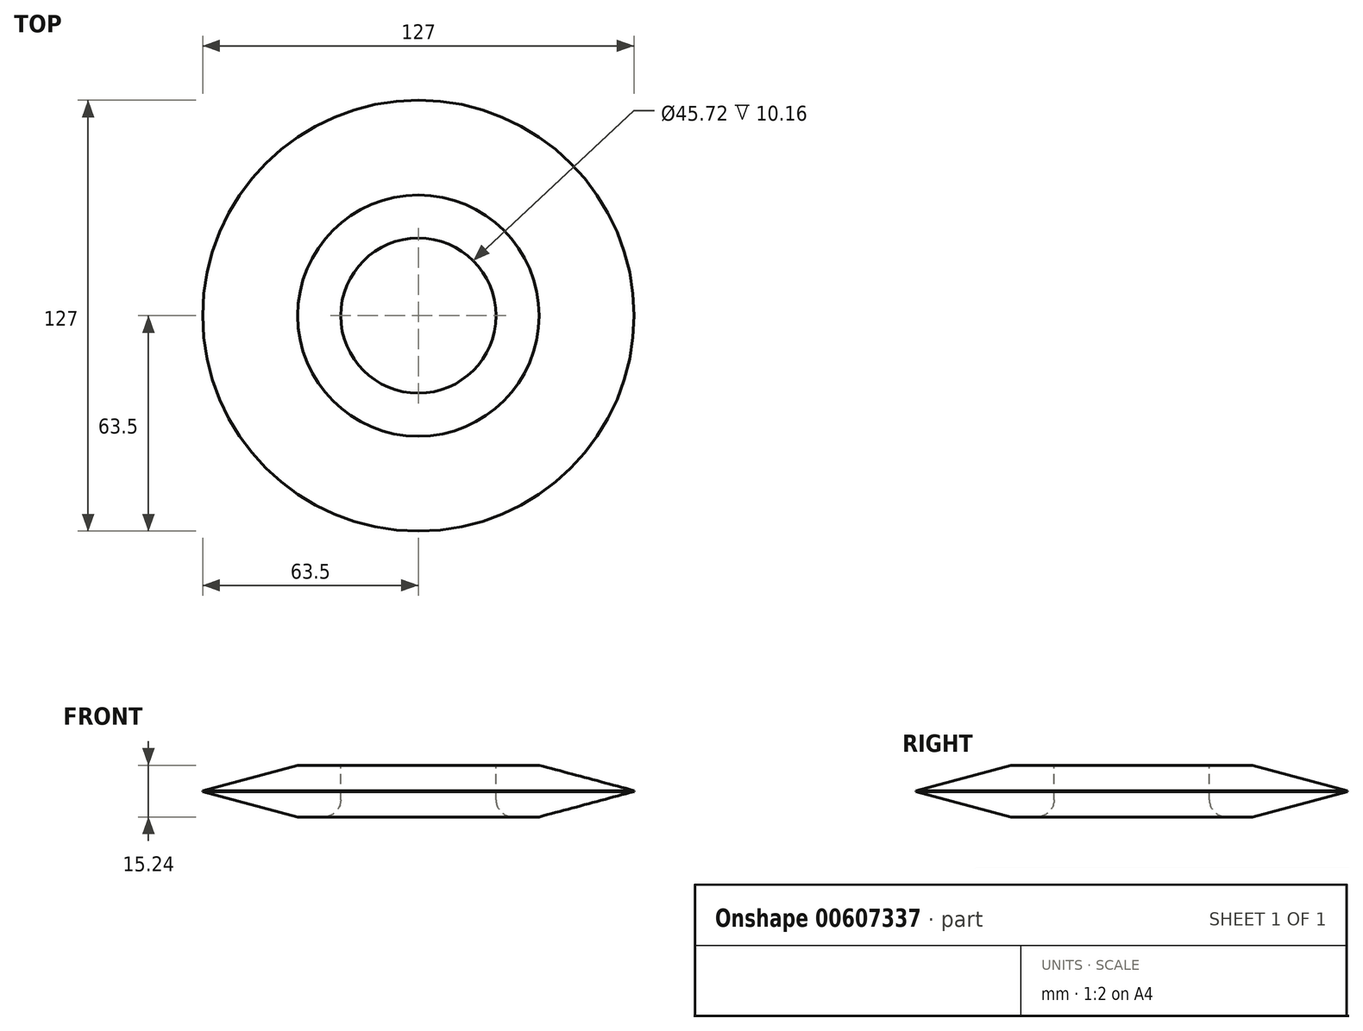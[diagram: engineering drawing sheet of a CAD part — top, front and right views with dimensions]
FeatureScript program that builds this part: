
annotation { "Feature Type Name" : "Feature", "Feature Type Description" : "" }
export const myFeature = defineFeature(function(context is Context, id is Id, definition is map)
    precondition{}
    {
        {
            var Q0;
            Q0=qCreatedBy(makeId("Top.planeOp"),FACE);
            var sketch = newSketch(context, id + "F0", { "sketchPlane" : qUnion([Q0])});
            skCircle(sketch, "E0", {"center": v(0, 0) * mm, "radius": 63.5 * mm});
            skSolve(sketch);
        }
        {
            var Q0;
            Q0 = qSketchRegion(id + "F0", true);
            extrude(context, id + "F1", {"entities" : qUnion([Q0]), "depth" : 15.24 * mm, "offsetDistance" : 25.4 * mm});
        }
        {
            var Q0;
            Q0=makeQuery(id+"F1.opExtrude","CAP_EDGE",EDGE,{"disambiguationData":[OSD([sQuery(id+"F0.wireOp",EDGE,"E0")])],"isStart":false});
            var Q1;
            Q1=makeQuery(id+"F1.opExtrude","SWEPT_FACE",FACE,{"disambiguationData":[OSD([sQuery(id+"F0.wireOp",EDGE,"E0")])]});
            chamfer(context, id + "F2", {"entities" : qUnion([Q0, Q1]), "chamferType" : ChamferType.OFFSET_ANGLE, "width" : 27.94 * mm, "oppositeDirection" : false, "angle" : 15 * degree, "tangentPropagation" : true});
        }
        {
            var Q0;
            Q0=makeQuery(id+"F1.opExtrude","CAP_FACE",FACE,{"disambiguationData":[OSD([sQuery(id+"F0.wireOp",EDGE,"E0")])],"isStart":false});
            var sketch = newSketch(context, id + "F3", { "sketchPlane" : qUnion([Q0])});
            skCircle(sketch, "E1", {"center": v(0, 0) * mm, "radius": 22.86 * mm});
            skSolve(sketch);
        }
        {
            var Q0;
            Q0 = qSketchRegion(id + "F3", true);
            extrude(context, id + "F4", {"entities" : qUnion([Q0]), "operationType" : NewBodyOperationType.REMOVE, "oppositeDirection" : true, "depth" : 25.4 * mm, "offsetDistance" : 25.4 * mm});
        }
        {
            var Q0;
            Q0=makeQuery(id+"F4.boolean.opBoolean","COPY",EDGE,{"derivedFrom":makeQuery(id+"F4.opExtrude","CAP_EDGE",EDGE,{"disambiguationData":[OSD([sQuery(id+"F3.wireOp",EDGE,"E1")])],"isStart":true})});
            var Q1;
            Q1=makeQuery(id+"F4.boolean.opBoolean","INTERSECT",EDGE,{"derivedFrom":[makeQuery(id+"F1.opExtrude","CAP_FACE",FACE,{"disambiguationData":[OSD([sQuery(id+"F0.wireOp",EDGE,"E0")])],"isStart":true}),makeQuery(id+"F4.opExtrude","SWEPT_FACE",FACE,{"disambiguationData":[OSD([sQuery(id+"F3.wireOp",EDGE,"E1")])]})]});
            fillet(context, id + "F5", {"entities" : qUnion([Q0, Q1]), "radius" : 5.08 * mm, "tangentPropagation" : true, "allowEdgeOverflow" : false});
        }
    });
